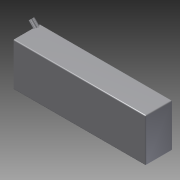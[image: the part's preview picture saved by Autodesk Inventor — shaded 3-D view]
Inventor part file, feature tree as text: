
AUTODESK INVENTOR PART (.ipt)
format: ipt  version: 2011 SP2 (Build 150309200, 309)  size: 123,904 bytes
history: native  units: mm
features: extrude x2, sketch x2, plane x1, fillet x1
ambient origin geometry x8: Origin, YZ Plane, XZ Plane, XY Plane, X Axis, Y Axis, Z Axis, Center Point
bodies: Solid1 (feature_tree)
feature tree (6):
  extrude  "Extrusion1"  Depth=28.0mm
  plane  "Work Plane1"
  extrude  "Extrusion2"  TaperAngle=135.0deg  [1 undecoded]
  fillet  "Fillet1"  Radius=3.0mm
  sketch  "Sketch1"  dims[d0=138.0mm d1=28.0mm]
  sketch  "Sketch2"  dims[d2=45.0mm d3=0.0mm d4=135.0deg d5=3.0mm d6=3.0mm d7=1.0mm d8=1.0mm d9=1.0mm d10=12.5mm d11=0.0mm d12=1.0mm]
note: 1 required parameter value undecoded (feature->parameter linkage not recoverable at this tier; creation-order binding heuristic only, values carry confidence <= 0.55)
